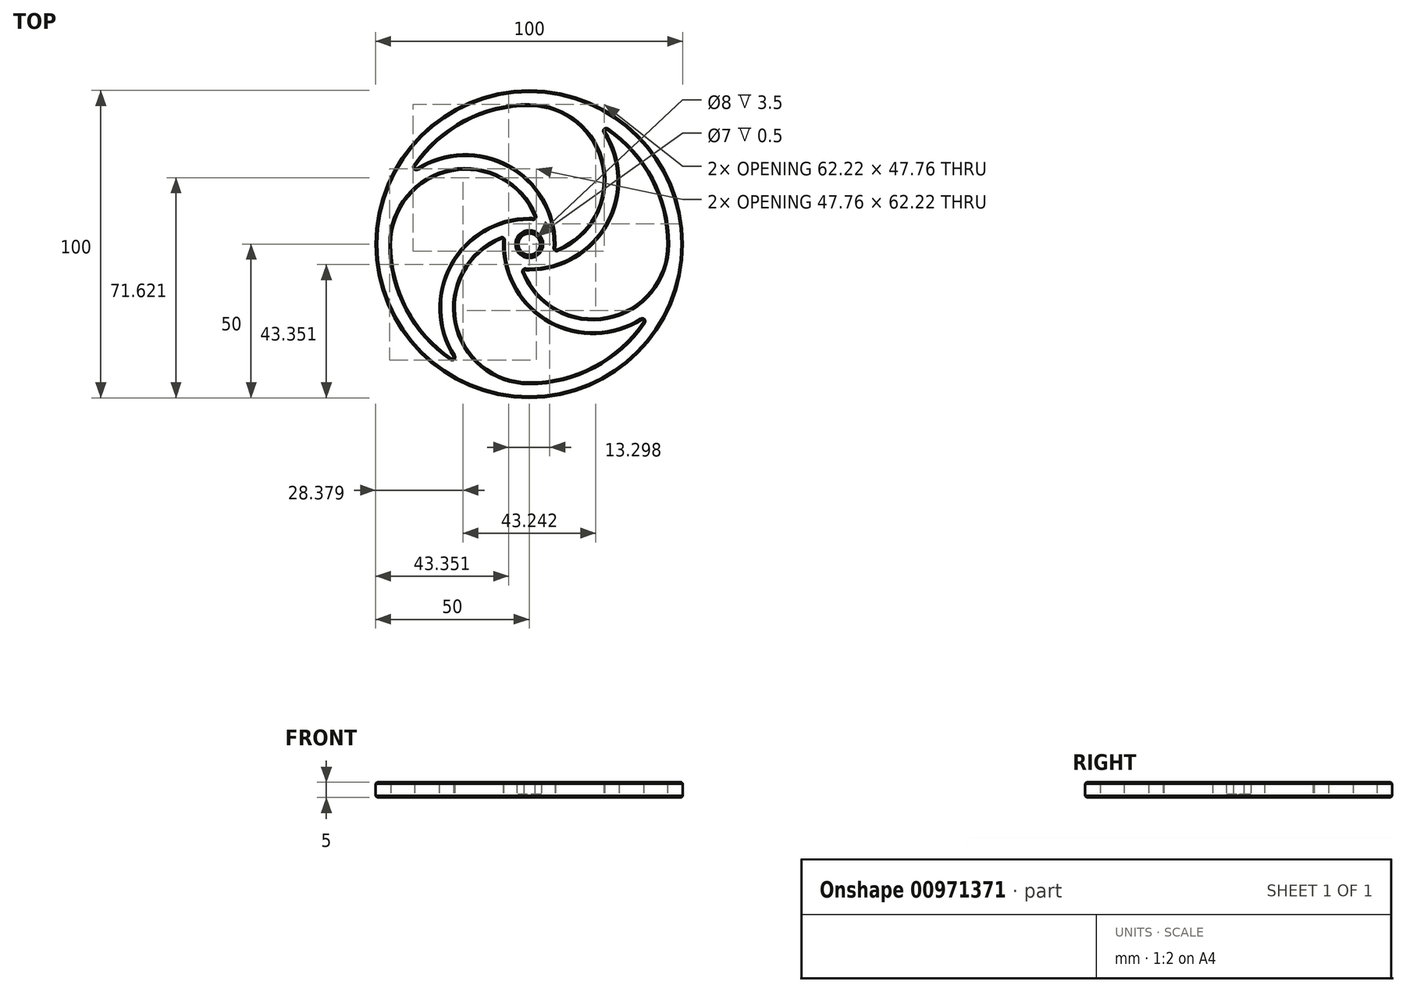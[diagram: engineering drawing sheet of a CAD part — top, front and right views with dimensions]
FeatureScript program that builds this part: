
annotation { "Feature Type Name" : "Feature", "Feature Type Description" : "" }
export const myFeature = defineFeature(function(context is Context, id is Id, definition is map)
    precondition{}
    {
        {
            var Q0;
            Q0=qCreatedBy(makeId("Top.planeOp"),FACE);
            var sketch = newSketch(context, id + "F0", { "sketchPlane" : qUnion([Q0])});
            skCircle(sketch, "E0", {"center": v(0, 0) * mm, "radius": 4 * mm});
            skCircle(sketch, "E1", {"center": v(0, 0) * mm, "radius": 7.5 * mm, "construction": true});
            skCircle(sketch, "E2.cCircle", {"center": v(0, 0) * mm, "radius": 50 * mm});
            skArc(sketch, "E3", {"start": v(0, 45) * mm, "mid": v(-22.14, 39.17) * mm, "end": v(-38.55, 23.2) * mm});
            skArc(sketch, "E4.cCircle", {"start": v(0, 45) * mm, "mid": v(-22.14, 39.17) * mm, "end": v(-38.55, 23.2) * mm, "construction": true});
            skLineSegment(sketch, "E4.0", {"start": v(0, 45) * mm, "end": v(38.97, -22.5) * mm, "construction": true});
            skLineSegment(sketch, "E4.1", {"start": v(38.97, -22.5) * mm, "end": v(-38.97, -22.5) * mm, "construction": true});
            skLineSegment(sketch, "E4.2", {"start": v(-38.97, -22.5) * mm, "end": v(0, 45) * mm, "construction": true});
            skPoint(sketch, "E5", {"position": v(0, 8.5) * mm});
            skArc(sketch, "E6.cCircle", {"start": v(-2.05, -8.25) * mm, "mid": v(-1.03, -8.44) * mm, "end": v(0, -8.5) * mm});
            skCircle(sketch, "E7", {"center": v(0, 0) * mm, "radius": 3.5 * mm, "construction": true});
            skPoint(sketch, "E8", {"position": v(0, -8.5) * mm});
            skPoint(sketch, "E9", {"position": v(0, 50) * mm});
            skLineSegment(sketch, "E10", {"start": v(0, 50) * mm, "end": v(0, -8.5) * mm, "construction": true});
            skArc(sketch, "E11.trimOffspring", {"start": v(0, -8.5) * mm, "mid": v(26.23, 7.81) * mm, "end": v(23.2, 38.55) * mm});
            skArc(sketch, "E12.trimOffspring", {"start": v(8.25, -2.05) * mm, "mid": v(23.89, 24.94) * mm, "end": v(0, 45) * mm});
            skArc(sketch, "E13.1.0", {"start": v(2.05, 8.25) * mm, "mid": v(-24.94, 23.89) * mm, "end": v(-45, 0) * mm});
            skArc(sketch, "E13.1.1", {"start": v(8.5, 0) * mm, "mid": v(-7.81, 26.23) * mm, "end": v(-38.55, 23.2) * mm});
            skArc(sketch, "E13.2.0", {"start": v(-8.25, 2.05) * mm, "mid": v(-23.89, -24.94) * mm, "end": v(0, -45) * mm});
            skArc(sketch, "E13.2.1", {"start": v(0, 8.5) * mm, "mid": v(-26.23, -7.81) * mm, "end": v(-23.2, -38.55) * mm});
            skArc(sketch, "E13.3.0", {"start": v(-2.05, -8.25) * mm, "mid": v(24.94, -23.89) * mm, "end": v(45, 0) * mm});
            skArc(sketch, "E13.3.1", {"start": v(-8.5, 0) * mm, "mid": v(7.81, -26.23) * mm, "end": v(38.55, -23.2) * mm});
            skArc(sketch, "E14.trimOffspring", {"start": v(-45, 0) * mm, "mid": v(-39.17, -22.14) * mm, "end": v(-23.2, -38.55) * mm, "construction": true});
            skArc(sketch, "E15.trimOffspring", {"start": v(-45, 0) * mm, "mid": v(-39.17, -22.14) * mm, "end": v(-23.2, -38.55) * mm});
            skArc(sketch, "E16.trimOffspring", {"start": v(0, -45) * mm, "mid": v(22.5, -38.97) * mm, "end": v(38.97, -22.5) * mm, "construction": true});
            skArc(sketch, "E17.trimOffspring", {"start": v(0, -45) * mm, "mid": v(22.5, -38.97) * mm, "end": v(38.97, -22.5) * mm});
            skArc(sketch, "E18.trimOffspring", {"start": v(45, 0) * mm, "mid": v(39.17, 22.14) * mm, "end": v(23.2, 38.55) * mm, "construction": true});
            skArc(sketch, "E19.trimOffspring", {"start": v(45, 0) * mm, "mid": v(39.17, 22.14) * mm, "end": v(23.2, 38.55) * mm});
            skArc(sketch, "E20.trimOffspring", {"start": v(-8.25, 2.05) * mm, "mid": v(-8.44, 1.03) * mm, "end": v(-8.5, 0) * mm});
            skArc(sketch, "E21.trimOffspring", {"start": v(2.05, 8.25) * mm, "mid": v(1.03, 8.44) * mm, "end": v(0, 8.5) * mm});
            skArc(sketch, "E22.trimOffspring", {"start": v(8.25, -2.05) * mm, "mid": v(8.44, -1.03) * mm, "end": v(8.5, 0) * mm});
            skSolve(sketch);
        }
        {
            var Q0;
            Q0=makeQuery(id+"F0.imprint","IMPRINT",FACE,{"disambiguationData":[TD([[makeQuery(id+"F0.imprint","IMPRINT",EDGE,{"derivedFrom":sQuery(id+"F0.wireOp",EDGE,"E0")}),-1.0]])]});
            extrude(context, id + "F1", {"entities" : qUnion([Q0]), "depth" : 5 * mm, "offsetDistance" : 25 * mm});
        }
        {
            var Q0;
            Q0=qCreatedBy(makeId("Top.planeOp"),FACE);
            var sketch = newSketch(context, id + "F2", { "sketchPlane" : qUnion([Q0])});
            skCircle(sketch, "E23", {"center": v(0, 0) * mm, "radius": 4 * mm});
            skCircle(sketch, "E24", {"center": v(0, 0) * mm, "radius": 3.5 * mm});
            skSolve(sketch);
        }
        {
            var Q0;
            Q0 = qSketchRegion(id + "F2", true);
            extrude(context, id + "F3", {"entities" : qUnion([Q0]), "depth" : 1 * mm, "offsetDistance" : 25 * mm});
        }
        {
            var Q0;
            Q0=makeQuery(id+"F1.opExtrude","SWEPT_BODY",BODY,{"disambiguationData":[OSD([sQuery(id+"F0.wireOp",EDGE,"E0"),sQuery(id+"F0.wireOp",EDGE,"E2.cCircle"),sQuery(id+"F0.wireOp",EDGE,"E3"),sQuery(id+"F0.wireOp",EDGE,"E6.cCircle"),sQuery(id+"F0.wireOp",EDGE,"E11.trimOffspring"),sQuery(id+"F0.wireOp",EDGE,"E12.trimOffspring"),sQuery(id+"F0.wireOp",EDGE,"E13.1.0"),sQuery(id+"F0.wireOp",EDGE,"E13.1.1"),sQuery(id+"F0.wireOp",EDGE,"E13.2.0"),sQuery(id+"F0.wireOp",EDGE,"E13.2.1"),sQuery(id+"F0.wireOp",EDGE,"E13.3.0"),sQuery(id+"F0.wireOp",EDGE,"E13.3.1"),sQuery(id+"F0.wireOp",EDGE,"E15.trimOffspring"),sQuery(id+"F0.wireOp",EDGE,"E17.trimOffspring"),sQuery(id+"F0.wireOp",EDGE,"E19.trimOffspring"),sQuery(id+"F0.wireOp",EDGE,"E20.trimOffspring"),sQuery(id+"F0.wireOp",EDGE,"E21.trimOffspring"),sQuery(id+"F0.wireOp",EDGE,"E22.trimOffspring")])]});
            var Q1;
            Q1=makeQuery(id+"F3.opExtrude","SWEPT_BODY",BODY,{"disambiguationData":[OSD([sQuery(id+"F2.wireOp",EDGE,"E23"),sQuery(id+"F2.wireOp",EDGE,"E24")])]});
            booleanBodies(context, id + "F4", {"operationType" : BooleanOperationType.UNION, "tools" : qUnion([Q0, Q1])});
        }
        {
            var Q0;
            Q0=makeQuery(id+"F1.opExtrude","SWEPT_EDGE",EDGE,{"disambiguationData":[OSD([sQuery(id+"F0.wireOp",EDGE,"E6.cCircle"),sQuery(id+"F0.wireOp",EDGE,"E13.3.0")])]});
            var Q1;
            Q1=makeQuery(id+"F1.opExtrude","SWEPT_EDGE",EDGE,{"disambiguationData":[OSD([sQuery(id+"F0.wireOp",EDGE,"E12.trimOffspring"),sQuery(id+"F0.wireOp",EDGE,"E22.trimOffspring")])]});
            var Q2;
            Q2=makeQuery(id+"F1.opExtrude","SWEPT_EDGE",EDGE,{"disambiguationData":[OSD([sQuery(id+"F0.wireOp",EDGE,"E3"),sQuery(id+"F0.wireOp",EDGE,"E13.1.1")])]});
            var Q3;
            Q3=makeQuery(id+"F1.opExtrude","SWEPT_EDGE",EDGE,{"disambiguationData":[OSD([sQuery(id+"F0.wireOp",EDGE,"E13.2.0"),sQuery(id+"F0.wireOp",EDGE,"E20.trimOffspring")])]});
            var Q4;
            Q4=makeQuery(id+"F1.opExtrude","SWEPT_EDGE",EDGE,{"disambiguationData":[OSD([sQuery(id+"F0.wireOp",EDGE,"E13.1.0"),sQuery(id+"F0.wireOp",EDGE,"E21.trimOffspring")])]});
            var Q5;
            Q5=makeQuery(id+"F1.opExtrude","SWEPT_EDGE",EDGE,{"disambiguationData":[OSD([sQuery(id+"F0.wireOp",EDGE,"E13.2.1"),sQuery(id+"F0.wireOp",EDGE,"E15.trimOffspring")])]});
            var Q6;
            Q6=makeQuery(id+"F1.opExtrude","SWEPT_EDGE",EDGE,{"disambiguationData":[OSD([sQuery(id+"F0.wireOp",EDGE,"E13.3.1"),sQuery(id+"F0.wireOp",EDGE,"E17.trimOffspring")])]});
            var Q7;
            Q7=makeQuery(id+"F1.opExtrude","SWEPT_EDGE",EDGE,{"disambiguationData":[OSD([sQuery(id+"F0.wireOp",EDGE,"E11.trimOffspring"),sQuery(id+"F0.wireOp",EDGE,"E19.trimOffspring")])]});
            fillet(context, id + "F5", {"entities" : qUnion([Q0, Q1, Q2, Q3, Q4, Q5, Q6, Q7]), "radius" : .5 * mm, "tangentPropagation" : true, "allowEdgeOverflow" : false});
        }
        {
            var Q0;
            Q0=makeQuery(id+"F1.opExtrude","CAP_FACE",FACE,{"disambiguationData":[OSD([sQuery(id+"F0.wireOp",EDGE,"E0"),sQuery(id+"F0.wireOp",EDGE,"E2.cCircle"),sQuery(id+"F0.wireOp",EDGE,"E3"),sQuery(id+"F0.wireOp",EDGE,"E6.cCircle"),sQuery(id+"F0.wireOp",EDGE,"E11.trimOffspring"),sQuery(id+"F0.wireOp",EDGE,"E12.trimOffspring"),sQuery(id+"F0.wireOp",EDGE,"E13.1.0"),sQuery(id+"F0.wireOp",EDGE,"E13.1.1"),sQuery(id+"F0.wireOp",EDGE,"E13.2.0"),sQuery(id+"F0.wireOp",EDGE,"E13.2.1"),sQuery(id+"F0.wireOp",EDGE,"E13.3.0"),sQuery(id+"F0.wireOp",EDGE,"E13.3.1"),sQuery(id+"F0.wireOp",EDGE,"E15.trimOffspring"),sQuery(id+"F0.wireOp",EDGE,"E17.trimOffspring"),sQuery(id+"F0.wireOp",EDGE,"E19.trimOffspring"),sQuery(id+"F0.wireOp",EDGE,"E20.trimOffspring"),sQuery(id+"F0.wireOp",EDGE,"E21.trimOffspring"),sQuery(id+"F0.wireOp",EDGE,"E22.trimOffspring")])],"isStart":false});
            var Q1;
            Q1=makeQuery(id+"F4.opBoolean","MERGE",FACE,{"derivedFrom":[makeQuery(id+"F1.opExtrude","CAP_FACE",FACE,{"disambiguationData":[OSD([sQuery(id+"F0.wireOp",EDGE,"E0"),sQuery(id+"F0.wireOp",EDGE,"E2.cCircle"),sQuery(id+"F0.wireOp",EDGE,"E3"),sQuery(id+"F0.wireOp",EDGE,"E6.cCircle"),sQuery(id+"F0.wireOp",EDGE,"E11.trimOffspring"),sQuery(id+"F0.wireOp",EDGE,"E12.trimOffspring"),sQuery(id+"F0.wireOp",EDGE,"E13.1.0"),sQuery(id+"F0.wireOp",EDGE,"E13.1.1"),sQuery(id+"F0.wireOp",EDGE,"E13.2.0"),sQuery(id+"F0.wireOp",EDGE,"E13.2.1"),sQuery(id+"F0.wireOp",EDGE,"E13.3.0"),sQuery(id+"F0.wireOp",EDGE,"E13.3.1"),sQuery(id+"F0.wireOp",EDGE,"E15.trimOffspring"),sQuery(id+"F0.wireOp",EDGE,"E17.trimOffspring"),sQuery(id+"F0.wireOp",EDGE,"E19.trimOffspring"),sQuery(id+"F0.wireOp",EDGE,"E20.trimOffspring"),sQuery(id+"F0.wireOp",EDGE,"E21.trimOffspring"),sQuery(id+"F0.wireOp",EDGE,"E22.trimOffspring")])],"isStart":true}),makeQuery(id+"F3.opExtrude","CAP_FACE",FACE,{"disambiguationData":[OSD([sQuery(id+"F2.wireOp",EDGE,"E23"),sQuery(id+"F2.wireOp",EDGE,"E24")])],"isStart":true})]});
            chamfer(context, id + "F6", {"entities" : qUnion([Q0, Q1]), "width" : .5 * mm, "tangentPropagation" : true});
        }
    });
